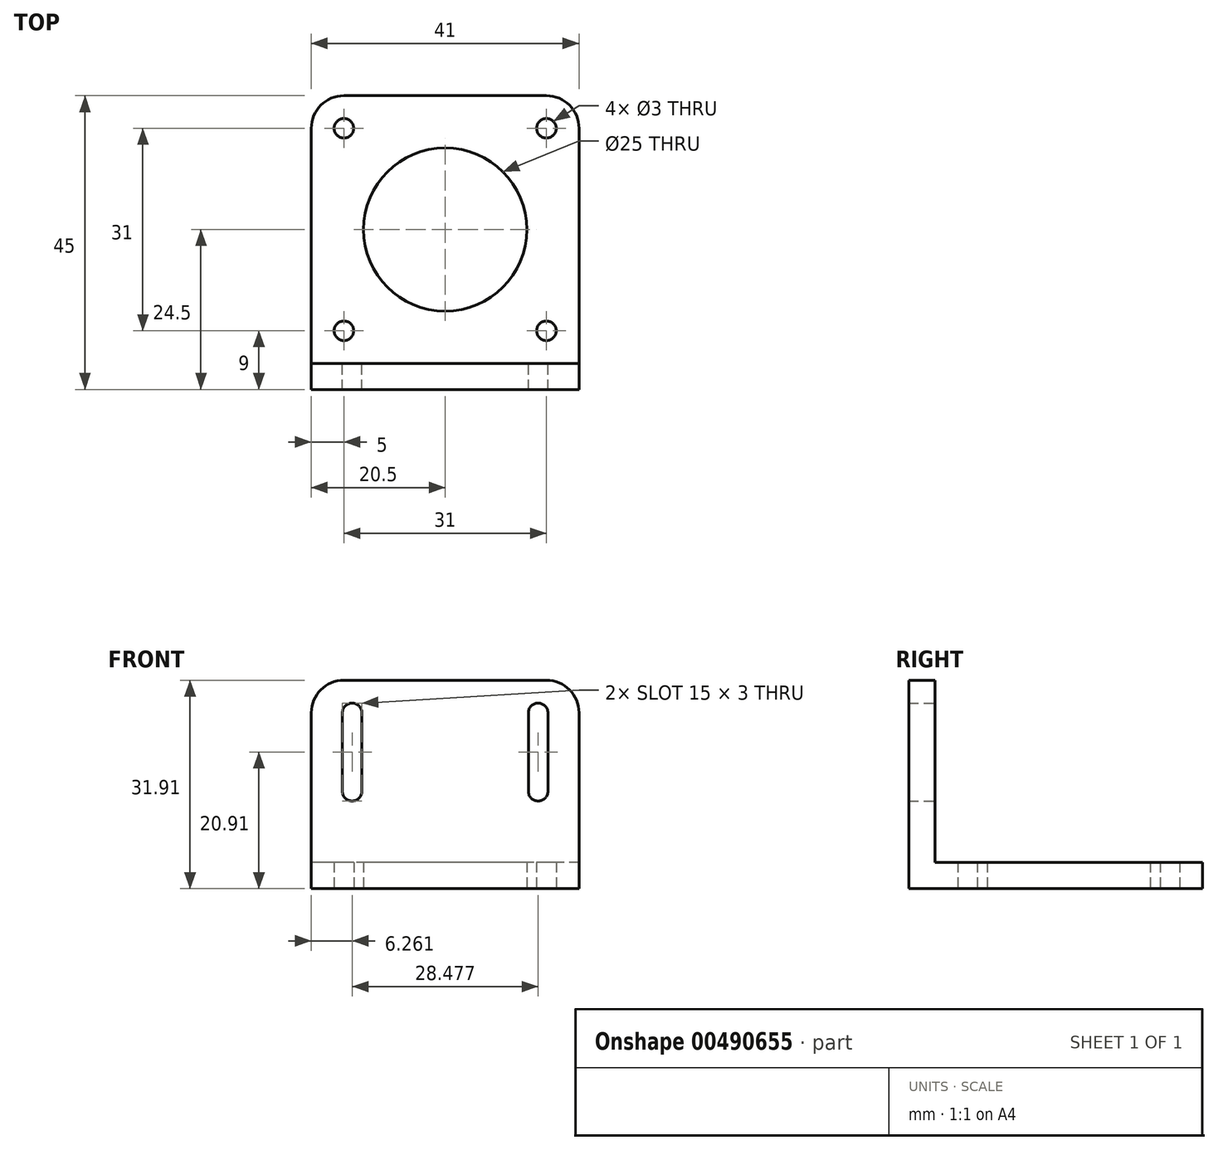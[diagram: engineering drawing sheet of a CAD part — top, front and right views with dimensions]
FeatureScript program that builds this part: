
annotation { "Feature Type Name" : "Feature", "Feature Type Description" : "" }
export const myFeature = defineFeature(function(context is Context, id is Id, definition is map)
    precondition{}
    {
        {
            var Q0;
            Q0=qCreatedBy(makeId("Top.planeOp"),FACE);
            var sketch = newSketch(context, id + "F0", { "sketchPlane" : qUnion([Q0])});
            skLineSegment(sketch, "E0.bottom", {"start": v(20.5, -20.5) * mm, "end": v(-20.5, -20.5) * mm});
            skLineSegment(sketch, "E0.top", {"start": v(20.5, 20.5) * mm, "end": v(-20.5, 20.5) * mm});
            skLineSegment(sketch, "E0.left", {"start": v(20.5, -20.5) * mm, "end": v(20.5, 20.5) * mm});
            skLineSegment(sketch, "E0.right", {"start": v(-20.5, -20.5) * mm, "end": v(-20.5, 20.5) * mm});
            skPoint(sketch, "E0.middle", {"position": v(0, 0) * mm});
            skCircle(sketch, "E1", {"center": v(-15.5, 15.5) * mm, "radius": 1.5 * mm});
            skLineSegment(sketch, "E2", {"start": v(-20.5, 20.5) * mm, "end": v(0, 0) * mm});
            skCircle(sketch, "E3.1.0", {"center": v(-15.5, -15.5) * mm, "radius": 1.5 * mm});
            skCircle(sketch, "E3.2.0", {"center": v(15.5, -15.5) * mm, "radius": 1.5 * mm});
            skCircle(sketch, "E3.3.0", {"center": v(15.5, 15.5) * mm, "radius": 1.5 * mm});
            skCircle(sketch, "E4", {"center": v(0, 0) * mm, "radius": 12.5 * mm});
            skSolve(sketch);
        }
        {
            var Q0;
            Q0=makeQuery(id+"F0.imprint","IMPRINT",FACE,{"disambiguationData":[TD([[makeQuery(id+"F0.imprint","IMPRINT",EDGE,{"derivedFrom":sQuery(id+"F0.wireOp",EDGE,"E0.bottom")}),-1.0]])]});
            extrude(context, id + "F1", {"entities" : qUnion([Q0]), "depth" : 4 * mm});
        }
        {
            var Q0;
            Q0=makeQuery(id+"F1.opExtrude","SWEPT_EDGE",EDGE,{"disambiguationData":[OSD([sQuery(id+"F0.wireOp",EDGE,"E0.top"),sQuery(id+"F0.wireOp",EDGE,"E0.right")])]});
            var Q1;
            Q1=makeQuery(id+"F1.opExtrude","SWEPT_EDGE",EDGE,{"disambiguationData":[OSD([sQuery(id+"F0.wireOp",EDGE,"E0.top"),sQuery(id+"F0.wireOp",EDGE,"E0.left")])]});
            fillet(context, id + "F2", {"entities" : qUnion([Q0, Q1]), "radius" : 5 * mm, "tangentPropagation" : true, "allowEdgeOverflow" : false});
        }
        {
            var Q0;
            Q0=makeQuery(id+"F1.opExtrude","SWEPT_FACE",FACE,{"disambiguationData":[OSD([sQuery(id+"F0.wireOp",EDGE,"E0.bottom")])]});
            var sketch = newSketch(context, id + "F3", { "sketchPlane" : qUnion([Q0])});
            skLineSegment(sketch, "E5.bottom", {"start": v(-20.5, 0) * mm, "end": v(20.5, 0) * mm});
            skLineSegment(sketch, "E5.top", {"start": v(-20.5, 31.9) * mm, "end": v(20.5, 31.9) * mm});
            skLineSegment(sketch, "E5.left", {"start": v(-20.5, 0) * mm, "end": v(-20.5, 31.9) * mm});
            skLineSegment(sketch, "E5.right", {"start": v(20.5, 0) * mm, "end": v(20.5, 31.9) * mm});
            skLineSegment(sketch, "E6.bottom", {"start": v(-15.74, 26.9) * mm, "end": v(-12.74, 26.9) * mm});
            skLineSegment(sketch, "E6.top", {"start": v(-15.74, 14.9) * mm, "end": v(-12.74, 14.9) * mm});
            skLineSegment(sketch, "E6.left", {"start": v(-15.74, 26.9) * mm, "end": v(-15.74, 14.9) * mm});
            skLineSegment(sketch, "E6.right", {"start": v(-12.74, 26.9) * mm, "end": v(-12.74, 14.9) * mm});
            skCircle(sketch, "E7", {"center": v(-14.24, 26.9) * mm, "radius": 1.5 * mm});
            skCircle(sketch, "E8", {"center": v(-14.24, 14.9) * mm, "radius": 1.5 * mm});
            skLineSegment(sketch, "E9", {"start": v(0, 31.9) * mm, "end": v(0, 0) * mm, "construction": true});
            skLineSegment(sketch, "E10.MirrorCS", {"start": v(15.74, 26.9) * mm, "end": v(12.74, 26.9) * mm});
            skLineSegment(sketch, "E11.MirrorCS", {"start": v(15.74, 26.9) * mm, "end": v(15.74, 14.9) * mm});
            skCircle(sketch, "E12.MirrorC", {"center": v(14.24, 14.9) * mm, "radius": 1.5 * mm});
            skLineSegment(sketch, "E13.MirrorCS", {"start": v(15.74, 14.9) * mm, "end": v(12.74, 14.9) * mm});
            skLineSegment(sketch, "E14.MirrorCS", {"start": v(12.74, 26.9) * mm, "end": v(12.74, 14.9) * mm});
            skCircle(sketch, "E15.MirrorC", {"center": v(14.24, 26.9) * mm, "radius": 1.5 * mm});
            skSolve(sketch);
        }
        {
            var Q0;
            {var subQ8=sQuery(id+"F3.wireOp",EDGE,"E5.top");Q0=makeQuery(id+"F3.imprint","IMPRINT",FACE,{"disambiguationData":[TD([[makeQuery(id+"F3.imprint","IMPRINT",EDGE,{"derivedFrom":subQ8}),-1.0]])]});}
            var Q1;
            {var subQ0=sQuery(id+"F3.wireOp",EDGE,"E5.bottom");Q1=makeQuery(id+"F3.imprint","IMPRINT",FACE,{"disambiguationData":[TD([[makeQuery(id+"F3.imprint","IMPRINT",EDGE,{"derivedFrom":subQ0}),-1.0]])]});}
            extrude(context, id + "F4", {"entities" : qUnion([Q0, Q1]), "operationType" : NewBodyOperationType.ADD, "depth" : 4 * mm});
        }
        {
            var Q0;
            Q0=makeQuery(id+"F4.opExtrude","SWEPT_EDGE",EDGE,{"disambiguationData":[OSD([sQuery(id+"F3.wireOp",EDGE,"E5.top"),sQuery(id+"F3.wireOp",EDGE,"E5.right")])]});
            var Q1;
            Q1=makeQuery(id+"F4.opExtrude","SWEPT_EDGE",EDGE,{"disambiguationData":[OSD([sQuery(id+"F3.wireOp",EDGE,"E5.top"),sQuery(id+"F3.wireOp",EDGE,"E5.left")])]});
            fillet(context, id + "F5", {"entities" : qUnion([Q0, Q1]), "radius" : 5 * mm, "tangentPropagation" : true, "allowEdgeOverflow" : false});
        }
    });
